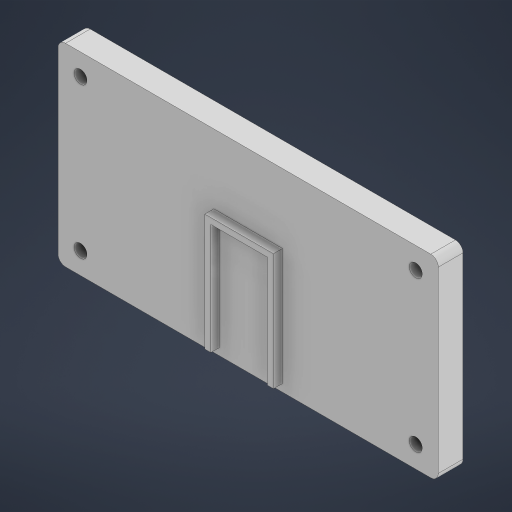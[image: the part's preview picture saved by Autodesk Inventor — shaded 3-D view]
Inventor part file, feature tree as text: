
AUTODESK INVENTOR PART (.ipt)
format: ipt  version: 2024.3 (Build 283343000, 343)  size: 329,728 bytes
history: native  units: mm
features: extrude x9, projected_geometry x8, sketch x7, fillet x1
ambient origin geometry x8: Origin, YZ Plane, XZ Plane, XY Plane, X Axis, Y Axis, Z Axis, Center Point
bodies: Body1 (feature_tree)
feature tree (25):
  sketch  "Sketch1"  dims[d0=126.85mm d1=64.605mm]
  extrude  "Extrusion2"  Depth=64.605mm
  extrude  "Extrusion3"  Depth=18.9mm
  extrude  "Extrusion4"  Depth=2.0mm
  extrude  "Extrusion5"  Depth=2.0mm
  fillet  "Fillet1"  Radius=5.235mm
  sketch  "Sketch3"  dims[d5=53.975mm d6=2.0mm]
  sketch  "Sketch4"  dims[d7=2.0mm d8=2.0mm d11=5.235mm d12=0.0mm]
  extrude  "Extrusion7"  Depth=8.235mm TaperAngle=0.0deg
  sketch  "Sketch5"  dims[d13=8.235mm d14=0.0mm d15=5.235mm d16=0.0mm]
  sketch  "Sketch6"  dims[d17=2.5mm d18=2.5mm]
  extrude  "Extrusion8"  Depth=2.5mm
  extrude  "Extrusion9"  Depth=2.5mm
  extrude  "Extrusion10"  Depth=10.0mm
  extrude  "Extrusion11"  Depth=10.0mm
  sketch  "Sketch2"  dims[d3=39.5mm d4=18.9mm]
  projected_geometry  "Projected Loop1"
  projected_geometry  "Projected Loop2"
  projected_geometry  "Projected Loop3"
  projected_geometry  "Projected Loop4"
  projected_geometry  "Projected Loop5"
  projected_geometry  "Projected Loop6"
  projected_geometry  "Projected Loop7"
  sketch  "Sketch7"  dims[d19=3.0mm d20=0.0mm d21=2.5mm d22=15.0mm d23=15.0mm d24=15.0mm d25=15.0mm d26=64.605mm d28=15.0mm d29=15.0mm d30=15.0mm d31=15.0mm d32=64.605mm d33=0.0mm d34=15.0mm d35=15.0mm d36=15.0mm d37=15.0mm d38=64.605mm d39=0.0mm d40=15.0mm d41=15.0mm d42=15.0mm d43=15.0mm d44=64.605mm d45=0.0mm d46=0.0mm d47=0.0mm d48=0.0mm d49=0.0mm d52=7.165mm d53=7.5mm d54=4.3mm d55=4.3mm d56=7.5mm d57=7.165mm d58=4.3mm d59=7.5mm d61=7.165mm d62=0.0mm d63=4.3mm d65=7.5mm d66=7.165mm d67=3.235mm d68=0.0mm d69=8.0mm d70=8.0mm d71=8.0mm d72=8.0mm d73=3.0mm d74=0.0mm d75=3.0mm d76=0.0mm d77=5.0mm d78=0.0mm d79=10.0mm d80=0.0mm]
  projected_geometry  "Projected Loop8"
